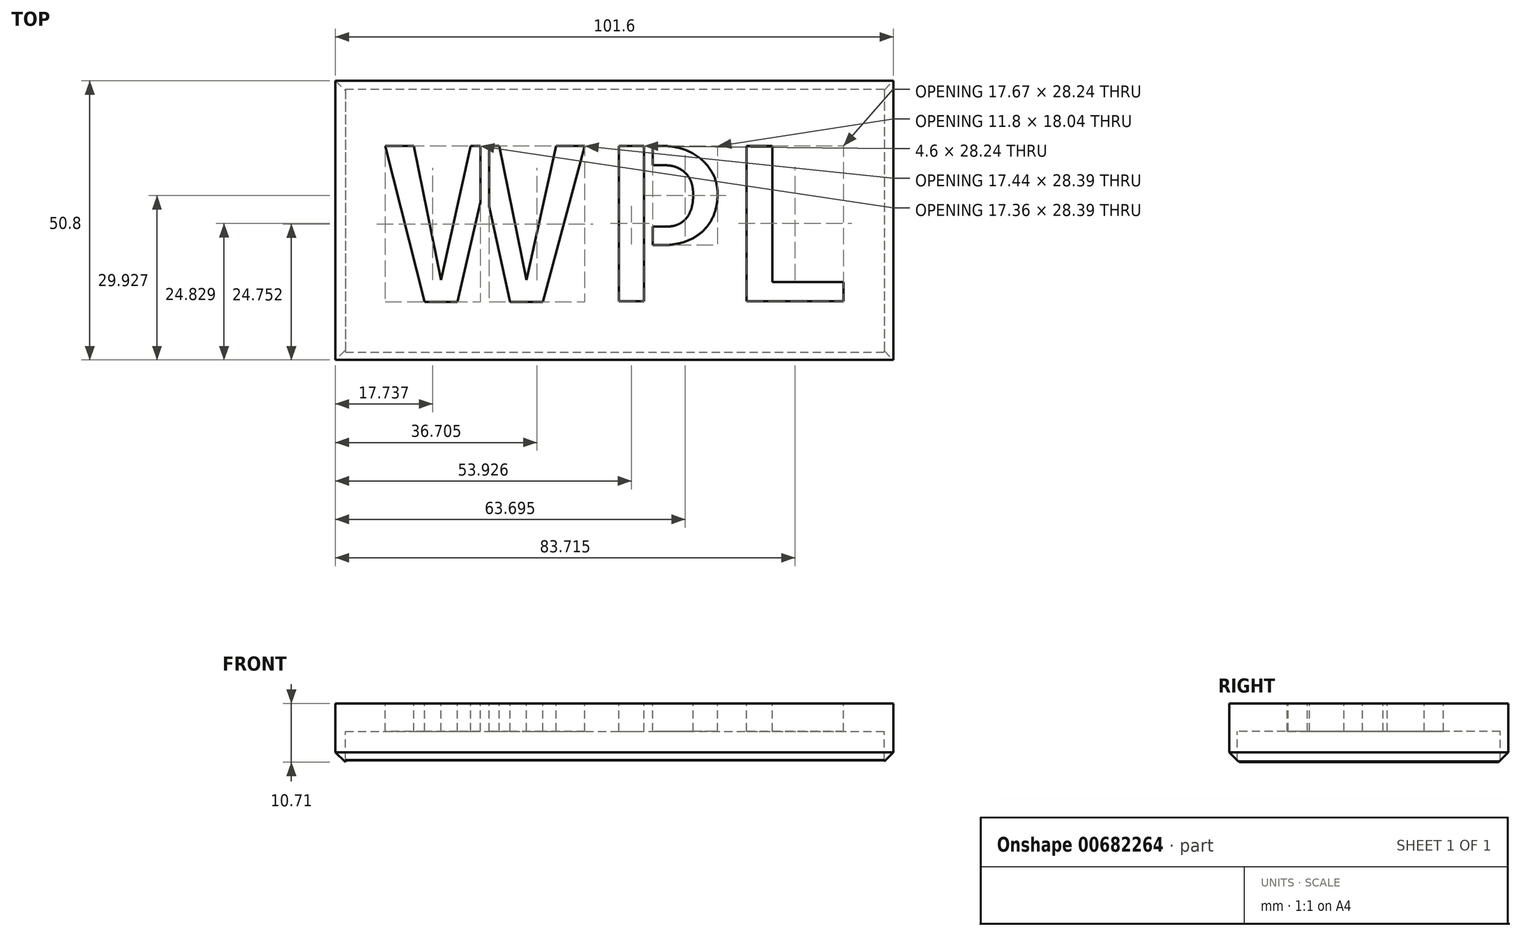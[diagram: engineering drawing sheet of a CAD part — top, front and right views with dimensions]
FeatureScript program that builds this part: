
annotation { "Feature Type Name" : "Feature", "Feature Type Description" : "" }
export const myFeature = defineFeature(function(context is Context, id is Id, definition is map)
    precondition{}
    {
        {
            var Q0;
            Q0=qCreatedBy(makeId("Top.planeOp"),FACE);
            var sketch = newSketch(context, id + "F0", { "sketchPlane" : qUnion([Q0])});
            skLineSegment(sketch, "E0.bottom", {"start": v(-65.88, 14.77) * mm, "end": v(35.72, 14.77) * mm});
            skLineSegment(sketch, "E0.top", {"start": v(-65.88, -36.03) * mm, "end": v(35.72, -36.03) * mm});
            skLineSegment(sketch, "E0.left", {"start": v(-65.88, 14.77) * mm, "end": v(-65.88, -36.03) * mm});
            skLineSegment(sketch, "E0.right", {"start": v(35.72, 14.77) * mm, "end": v(35.72, -36.03) * mm});
            skLineSegment(sketch, "E1.bottom", {"start": v(-64.07, 13.27) * mm, "end": v(34.06, 13.27) * mm});
            skLineSegment(sketch, "E1.top", {"start": v(-64.07, -34.6) * mm, "end": v(34.06, -34.6) * mm});
            skLineSegment(sketch, "E1.left", {"start": v(-64.07, 13.27) * mm, "end": v(-64.07, -34.6) * mm});
            skLineSegment(sketch, "E1.right", {"start": v(34.06, 13.27) * mm, "end": v(34.06, -34.6) * mm});
            skSolve(sketch);
        }
        {
            var Q0;
            Q0=makeQuery(id+"F0.imprint","IMPRINT",FACE,{"disambiguationData":[TD([[makeQuery(id+"F0.imprint","IMPRINT",EDGE,{"derivedFrom":sQuery(id+"F0.wireOp",EDGE,"E1.bottom")}),-1.0]])]});
            var Q1;
            Q1=makeQuery(id+"F0.imprint","IMPRINT",FACE,{"disambiguationData":[TD([[makeQuery(id+"F0.imprint","IMPRINT",EDGE,{"derivedFrom":sQuery(id+"F0.wireOp",EDGE,"E0.bottom")}),-1.0]])]});
            extrude(context, id + "F1", {"entities" : qUnion([Q0, Q1]), "depth" : 5.08 * mm, "offsetDistance" : 25.4 * mm});
        }
        {
            var Q0;
            Q0 = qSketchRegion(id + "F0", true);
            extrude(context, id + "F2", {"entities" : qUnion([Q0]), "operationType" : NewBodyOperationType.ADD, "oppositeDirection" : true, "depth" : 6.35 * mm, "offsetDistance" : 25.4 * mm});
        }
        {
            var Q0;
            Q0=makeQuery(id+"F1.opExtrude","CAP_FACE",FACE,{"disambiguationData":[OSD([sQuery(id+"F0.wireOp",EDGE,"E0.bottom"),sQuery(id+"F0.wireOp",EDGE,"E0.top"),sQuery(id+"F0.wireOp",EDGE,"E0.left"),sQuery(id+"F0.wireOp",EDGE,"E0.right")])],"isStart":false});
            var sketch = newSketch(context, id + "F3", { "sketchPlane" : qUnion([Q0])});
            skText(sketch, "E2", { "text": "WPL", "fontName": "AllertaStencil-Regular.ttf"});
            const initialGuessF3  = {"E2": [-0.05962, -0.02532, 1, 0, 0.02825]};
            skSetInitialGuess(sketch, initialGuessF3);
            skSolve(sketch);
        }
        {
            var Q0;
            Q0 = qSketchRegion(id + "F3", true);
            extrude(context, id + "F4", {"entities" : qUnion([Q0]), "operationType" : NewBodyOperationType.REMOVE, "oppositeDirection" : true, "depth" : 25.4 * mm, "offsetDistance" : 25.4 * mm});
        }
        {
            var Q0;
            Q0=makeQuery(id+"F2.opExtrude","CAP_EDGE",EDGE,{"disambiguationData":[OSD([sQuery(id+"F0.wireOp",EDGE,"E0.left")])],"isStart":false});
            var Q1;
            Q1=makeQuery(id+"F2.opExtrude","CAP_EDGE",EDGE,{"disambiguationData":[OSD([sQuery(id+"F0.wireOp",EDGE,"E0.top")])],"isStart":false});
            var Q2;
            Q2=makeQuery(id+"F2.opExtrude","CAP_EDGE",EDGE,{"disambiguationData":[OSD([sQuery(id+"F0.wireOp",EDGE,"E0.right")])],"isStart":false});
            var Q3;
            Q3=makeQuery(id+"F2.opExtrude","CAP_EDGE",EDGE,{"disambiguationData":[OSD([sQuery(id+"F0.wireOp",EDGE,"E0.bottom")])],"isStart":false});
            chamfer(context, id + "F5", {"entities" : qUnion([Q0, Q1, Q2, Q3]), "width" : 2.54 * mm, "tangentPropagation" : true});
        }
    });
